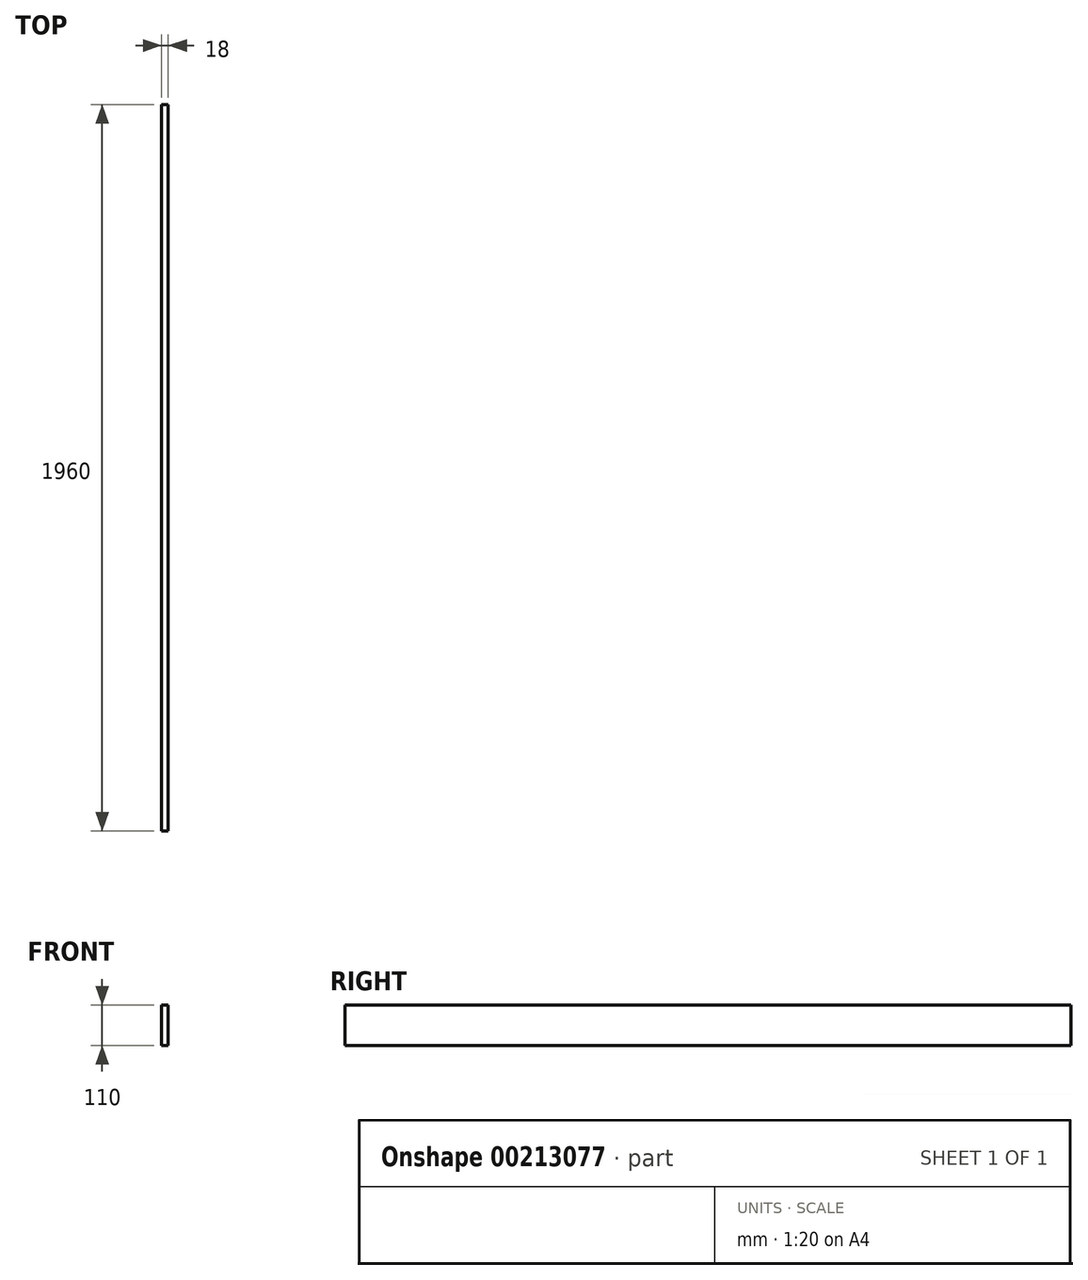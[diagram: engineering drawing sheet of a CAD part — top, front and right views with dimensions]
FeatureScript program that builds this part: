
annotation { "Feature Type Name" : "Feature", "Feature Type Description" : "" }
export const myFeature = defineFeature(function(context is Context, id is Id, definition is map)
    precondition{}
    {
        {
            var Q0;
            Q0=qCreatedBy(makeId("Right.planeOp"),FACE);
            var sketch = newSketch(context, id + "F0", { "sketchPlane" : qUnion([Q0])});
            skLineSegment(sketch, "E0.bottom", {"start": v(-980, 55) * mm, "end": v(980, 55) * mm});
            skLineSegment(sketch, "E0.top", {"start": v(-980, -55) * mm, "end": v(980, -55) * mm});
            skLineSegment(sketch, "E0.left", {"start": v(-980, 55) * mm, "end": v(-980, -55) * mm});
            skLineSegment(sketch, "E0.right", {"start": v(980, 55) * mm, "end": v(980, -55) * mm});
            skPoint(sketch, "E0.middle", {"position": v(0, 0) * mm});
            skSolve(sketch);
        }
        {
            var Q0;
            Q0=makeQuery(id+"F0.imprint","IMPRINT",FACE,{"disambiguationData":[TD([[makeQuery(id+"F0.imprint","IMPRINT",EDGE,{"derivedFrom":sQuery(id+"F0.wireOp",EDGE,"E0.bottom")}),-1.0]])]});
            extrude(context, id + "F1", {"entities" : qUnion([Q0]), "endBound" : BoundingType.SYMMETRIC, "depth" : 18 * mm});
        }
    });
